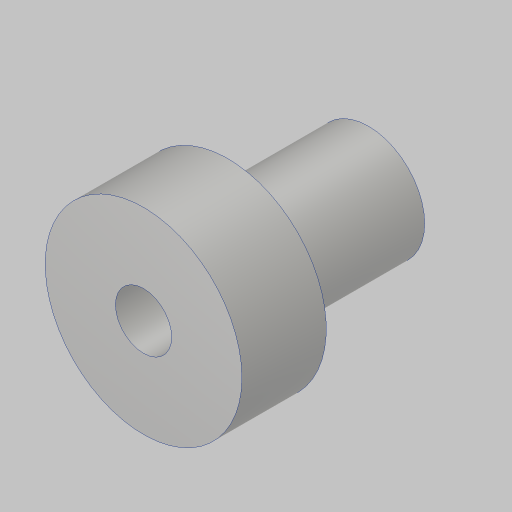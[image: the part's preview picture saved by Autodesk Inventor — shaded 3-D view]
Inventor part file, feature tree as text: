
AUTODESK INVENTOR PART (.ipt)
format: ipt  version: 2023.5 (Build 275446000, 446)  size: 119,296 bytes
history: native  units: in
note: dims shown in document units (in); Inventor stores cm internally (conversion verified against a paired STEP export)
features: sketch x3, extrude x2, hole x1, projected_geometry x1
ambient origin geometry x8: Origin, YZ Plane, XZ Plane, XY Plane, X Axis, Y Axis, Z Axis, Center Point
bodies: Solid1 (feature_tree)
feature tree (7):
  extrude  "Extrusion1"  Depth=1.0in TaperAngle=0.0deg
  extrude  "Extrusion3"  Depth=0.625in TaperAngle=0.0deg
  hole  "Hole2"  [1 undecoded]
  sketch  "Sketch1"  dims[d0=0.875in d1=1.0in d2=0.0in]
  sketch  "Sketch3"  dims[d6=0.5in d7=0.625in d8=0.0in]
  projected_geometry  "Projected Loop2"
  sketch  "Sketch5"  dims[d17=0.25in d18=0.75in d19=0.279in d20=0.25in d21=0.5635in d22=1.0in d23=0.8108in]
note: 1 required parameter value undecoded (feature->parameter linkage not recoverable at this tier; creation-order binding heuristic only, values carry confidence <= 0.55)
